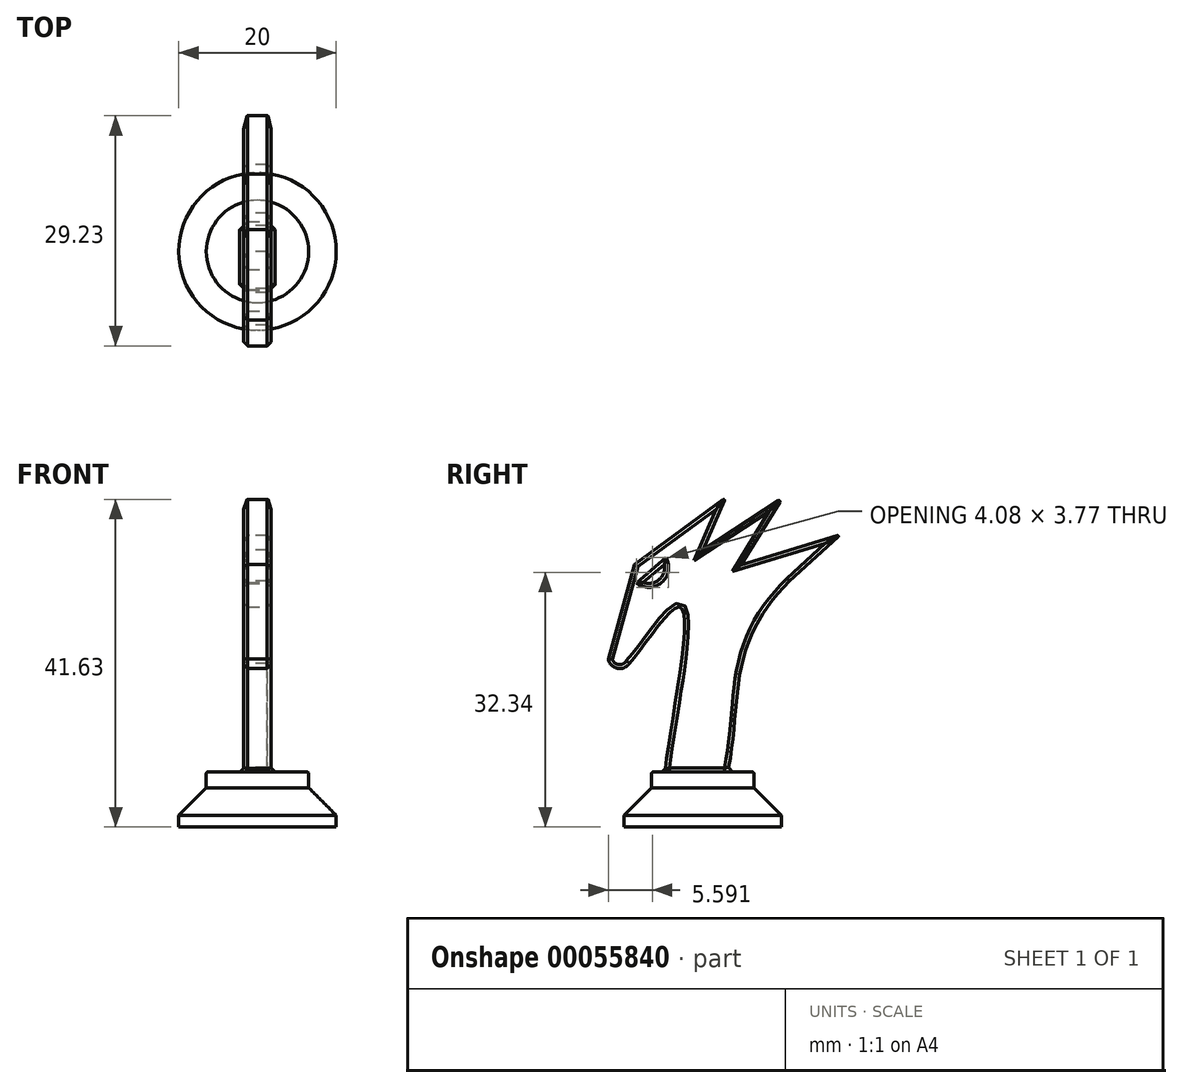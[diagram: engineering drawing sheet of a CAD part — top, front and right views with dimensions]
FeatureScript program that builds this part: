
annotation { "Feature Type Name" : "Feature", "Feature Type Description" : "" }
export const myFeature = defineFeature(function(context is Context, id is Id, definition is map)
    precondition{}
    {
        {
            var Q0;
            Q0=qCreatedBy(makeId("Top.planeOp"),FACE);
            var sketch = newSketch(context, id + "F0", { "sketchPlane" : qUnion([Q0])});
            skCircle(sketch, "E0", {"center": v(0, 0) * mm, "radius": 10 * mm});
            skSolve(sketch);
        }
        {
            var Q0;
            Q0=makeQuery(id+"F0.imprint","IMPRINT",FACE,{"disambiguationData":[TD([[makeQuery(id+"F0.imprint","IMPRINT",EDGE,{"derivedFrom":sQuery(id+"F0.wireOp",EDGE,"E0")}),1.0]])]});
            extrude(context, id + "F1", {"entities" : qUnion([Q0]), "depth" : 5 * mm});
        }
        {
            var Q0;
            Q0=makeQuery(id+"F1.opExtrude","CAP_EDGE",EDGE,{"disambiguationData":[OSD([sQuery(id+"F0.wireOp",EDGE,"E0")])],"isStart":false});
            chamfer(context, id + "F2", {"entities" : qUnion([Q0]), "width" : 3.5 * mm, "tangentPropagation" : true});
        }
        {
            var Q0;
            Q0=makeQuery(id+"F1.opExtrude","CAP_FACE",FACE,{"disambiguationData":[OSD([sQuery(id+"F0.wireOp",EDGE,"E0")])],"isStart":false});
            var sketch = newSketch(context, id + "F3", { "sketchPlane" : qUnion([Q0])});
            skCircle(sketch, "E1.0.0", {"center": v(0, 0) * mm, "radius": 6.5 * mm});
            skSolve(sketch);
        }
        {
            var Q0;
            Q0=makeQuery(id+"F3.imprint","IMPRINT",FACE,{"disambiguationData":[TD([[makeQuery(id+"F3.imprint","IMPRINT",EDGE,{"derivedFrom":sQuery(id+"F3.wireOp",EDGE,"E1.0.0")}),1.0]])]});
            extrude(context, id + "F4", {"entities" : qUnion([Q0]), "operationType" : NewBodyOperationType.ADD, "depth" : 2 * mm});
        }
        {
            var Q0;
            Q0=qCreatedBy(makeId("Right.planeOp"),FACE);
            var sketch = newSketch(context, id + "F5", { "sketchPlane" : qUnion([Q0])});
            skLineSegment(sketch, "E2.0.0", {"start": v(-6.5, 7) * mm, "end": v(6.5, 7) * mm});
            skFitSpline(sketch, "E3", {"points": [v(-4.74, 7) * mm, v(-2.8, 27.91) * mm, v(-9.33, 20.82) * mm], "startDerivative": vector(1.1, 22.43) * mm, "endDerivative": vector(-12.77, -13.23) * mm});
            skArc(sketch, "E4", {"start": v(-12, 21.37) * mm, "mid": v(-10.86, 20.16) * mm, "end": v(-9.33, 20.82) * mm});
            skLineSegment(sketch, "E5", {"start": v(-12, 21.37) * mm, "end": v(-8.69, 33.4) * mm});
            skLineSegment(sketch, "E6", {"start": v(-8.69, 33.4) * mm, "end": v(2.9, 41.83) * mm});
            skLineSegment(sketch, "E7", {"start": v(2.9, 41.83) * mm, "end": v(0, 35.22) * mm});
            skLineSegment(sketch, "E8", {"start": v(0, 35.22) * mm, "end": v(10.02, 41.7) * mm});
            skLineSegment(sketch, "E9", {"start": v(10.02, 41.7) * mm, "end": v(4.89, 33.33) * mm});
            skLineSegment(sketch, "E10", {"start": v(4.89, 33.33) * mm, "end": v(17.52, 37.16) * mm});
            skLineSegment(sketch, "E11", {"start": v(17.52, 37.16) * mm, "end": v(11.03, 31.24) * mm});
            skFitSpline(sketch, "E12", {"points": [v(3.17, 7) * mm, v(5.13, 21.39) * mm, v(11.03, 31.24) * mm], "startDerivative": vector(6.07, 28) * mm, "endDerivative": vector(18.53, 18.29) * mm});
            skSolve(sketch);
        }
        {
            var Q0;
            {var subQ0=sQuery(id+"F5.wireOp",EDGE,"E3");Q0=makeQuery(id+"F5.imprint","IMPRINT",FACE,{"disambiguationData":[TD([[makeQuery(id+"F5.imprint","IMPRINT",EDGE,{"derivedFrom":subQ0}),-1.0]])]});}
            extrude(context, id + "F6", {"entities" : qUnion([Q0]), "operationType" : NewBodyOperationType.ADD, "endBound" : BoundingType.SYMMETRIC, "depth" : 3.5 * mm});
        }
        {
            var Q0;
            Q0=makeQuery(id+"F6.opExtrude","CAP_FACE",FACE,{"disambiguationData":[OSD([sQuery(id+"F5.wireOp",EDGE,"E2.0.0"),sQuery(id+"F5.wireOp",EDGE,"E3"),sQuery(id+"F5.wireOp",EDGE,"E4"),sQuery(id+"F5.wireOp",EDGE,"E5"),sQuery(id+"F5.wireOp",EDGE,"E6"),sQuery(id+"F5.wireOp",EDGE,"E7"),sQuery(id+"F5.wireOp",EDGE,"E8"),sQuery(id+"F5.wireOp",EDGE,"E9"),sQuery(id+"F5.wireOp",EDGE,"E10"),sQuery(id+"F5.wireOp",EDGE,"E11"),sQuery(id+"F5.wireOp",EDGE,"E12")])],"isStart":false});
            var sketch = newSketch(context, id + "F7", { "sketchPlane" : qUnion([Q0])});
            skFitSpline(sketch, "E13.0.0", {"points": [v(-9.33, 20.82) * mm, v(-7.61, 22.6) * mm, v(1.35, 37.4) * mm, v(-4.52, 11.46) * mm, v(-4.74, 7) * mm]});
            skLineSegment(sketch, "E13.0.1", {"start": v(-4.74, 7) * mm, "end": v(3.17, 7) * mm});
            skFitSpline(sketch, "E13.0.2", {"points": [v(3.17, 7) * mm, v(4.24, 11.94) * mm, v(3.84, 21.66) * mm, v(8.13, 28.37) * mm, v(11.03, 31.24) * mm]});
            skLineSegment(sketch, "E13.0.3", {"start": v(11.03, 31.24) * mm, "end": v(17.52, 37.16) * mm});
            skLineSegment(sketch, "E13.0.4", {"start": v(17.52, 37.16) * mm, "end": v(4.89, 33.33) * mm});
            skLineSegment(sketch, "E13.0.5", {"start": v(4.89, 33.33) * mm, "end": v(10.02, 41.7) * mm});
            skLineSegment(sketch, "E13.0.6", {"start": v(10.02, 41.7) * mm, "end": v(0, 35.22) * mm});
            skLineSegment(sketch, "E13.0.7", {"start": v(0, 35.22) * mm, "end": v(2.9, 41.83) * mm});
            skLineSegment(sketch, "E13.0.8", {"start": v(2.9, 41.83) * mm, "end": v(-8.69, 33.4) * mm});
            skLineSegment(sketch, "E13.0.9", {"start": v(-8.69, 33.4) * mm, "end": v(-12, 21.37) * mm});
            skArc(sketch, "E13.0.10", {"start": v(-12, 21.37) * mm, "mid": v(-10.86, 20.16) * mm, "end": v(-9.33, 20.82) * mm});
            skLineSegment(sketch, "E14", {"start": v(-4.88, 33.4) * mm, "end": v(-7.6, 31.1) * mm});
            skArc(sketch, "E15", {"start": v(-7.6, 31.1) * mm, "mid": v(-5.55, 31.43) * mm, "end": v(-4.88, 33.4) * mm});
            skSolve(sketch);
        }
        {
            var Q0;
            Q0=makeQuery(id+"F7.imprint","IMPRINT",FACE,{"disambiguationData":[TD([[makeQuery(id+"F7.imprint","IMPRINT",EDGE,{"derivedFrom":sQuery(id+"F7.wireOp",EDGE,"E14")}),1.0]])]});
            extrude(context, id + "F8", {"entities" : qUnion([Q0]), "operationType" : NewBodyOperationType.REMOVE, "endBound" : BoundingType.THROUGH_ALL, "oppositeDirection" : true, "depth" : 25 * mm});
        }
        {
            var Q0;
            Q0=makeQuery(id+"F6.opExtrude","CAP_FACE",FACE,{"disambiguationData":[OSD([sQuery(id+"F5.wireOp",EDGE,"E2.0.0"),sQuery(id+"F5.wireOp",EDGE,"E3"),sQuery(id+"F5.wireOp",EDGE,"E4"),sQuery(id+"F5.wireOp",EDGE,"E5"),sQuery(id+"F5.wireOp",EDGE,"E6"),sQuery(id+"F5.wireOp",EDGE,"E7"),sQuery(id+"F5.wireOp",EDGE,"E8"),sQuery(id+"F5.wireOp",EDGE,"E9"),sQuery(id+"F5.wireOp",EDGE,"E10"),sQuery(id+"F5.wireOp",EDGE,"E11"),sQuery(id+"F5.wireOp",EDGE,"E12")])],"isStart":false});
            var Q1;
            Q1=makeQuery(id+"F6.opExtrude","CAP_FACE",FACE,{"disambiguationData":[OSD([sQuery(id+"F5.wireOp",EDGE,"E2.0.0"),sQuery(id+"F5.wireOp",EDGE,"E3"),sQuery(id+"F5.wireOp",EDGE,"E4"),sQuery(id+"F5.wireOp",EDGE,"E5"),sQuery(id+"F5.wireOp",EDGE,"E6"),sQuery(id+"F5.wireOp",EDGE,"E7"),sQuery(id+"F5.wireOp",EDGE,"E8"),sQuery(id+"F5.wireOp",EDGE,"E9"),sQuery(id+"F5.wireOp",EDGE,"E10"),sQuery(id+"F5.wireOp",EDGE,"E11"),sQuery(id+"F5.wireOp",EDGE,"E12")])],"isStart":true});
            chamfer(context, id + "F9", {"entities" : qUnion([Q0, Q1]), "width" : .5 * mm, "tangentPropagation" : true});
        }
        {
            var Q0;
            Q0=makeQuery(id+"F6.opExtrude","SWEPT_EDGE",EDGE,{"disambiguationData":[OSD([sQuery(id+"F5.wireOp",EDGE,"E10"),sQuery(id+"F5.wireOp",EDGE,"E11")])]});
            var Q1;
            Q1=makeQuery(id+"F6.opExtrude","SWEPT_EDGE",EDGE,{"disambiguationData":[OSD([sQuery(id+"F5.wireOp",EDGE,"E8"),sQuery(id+"F5.wireOp",EDGE,"E9")])]});
            var Q2;
            Q2=makeQuery(id+"F6.opExtrude","SWEPT_EDGE",EDGE,{"disambiguationData":[OSD([sQuery(id+"F5.wireOp",EDGE,"E6"),sQuery(id+"F5.wireOp",EDGE,"E7")])]});
            fillet(context, id + "F10", {"entities" : qUnion([Q0, Q1, Q2]), "radius" : .1 * mm, "tangentPropagation" : true, "allowEdgeOverflow" : false});
        }
        {
            var Q0;
            Q0=makeQuery(id+"F4.opExtrude","CAP_EDGE",EDGE,{"disambiguationData":[OSD([sQuery(id+"F3.wireOp",EDGE,"E1.0.0")])],"isStart":false});
            fillet(context, id + "F11", {"entities" : qUnion([Q0]), "radius" : .2 * mm, "tangentPropagation" : true, "allowEdgeOverflow" : false});
        }
    });
